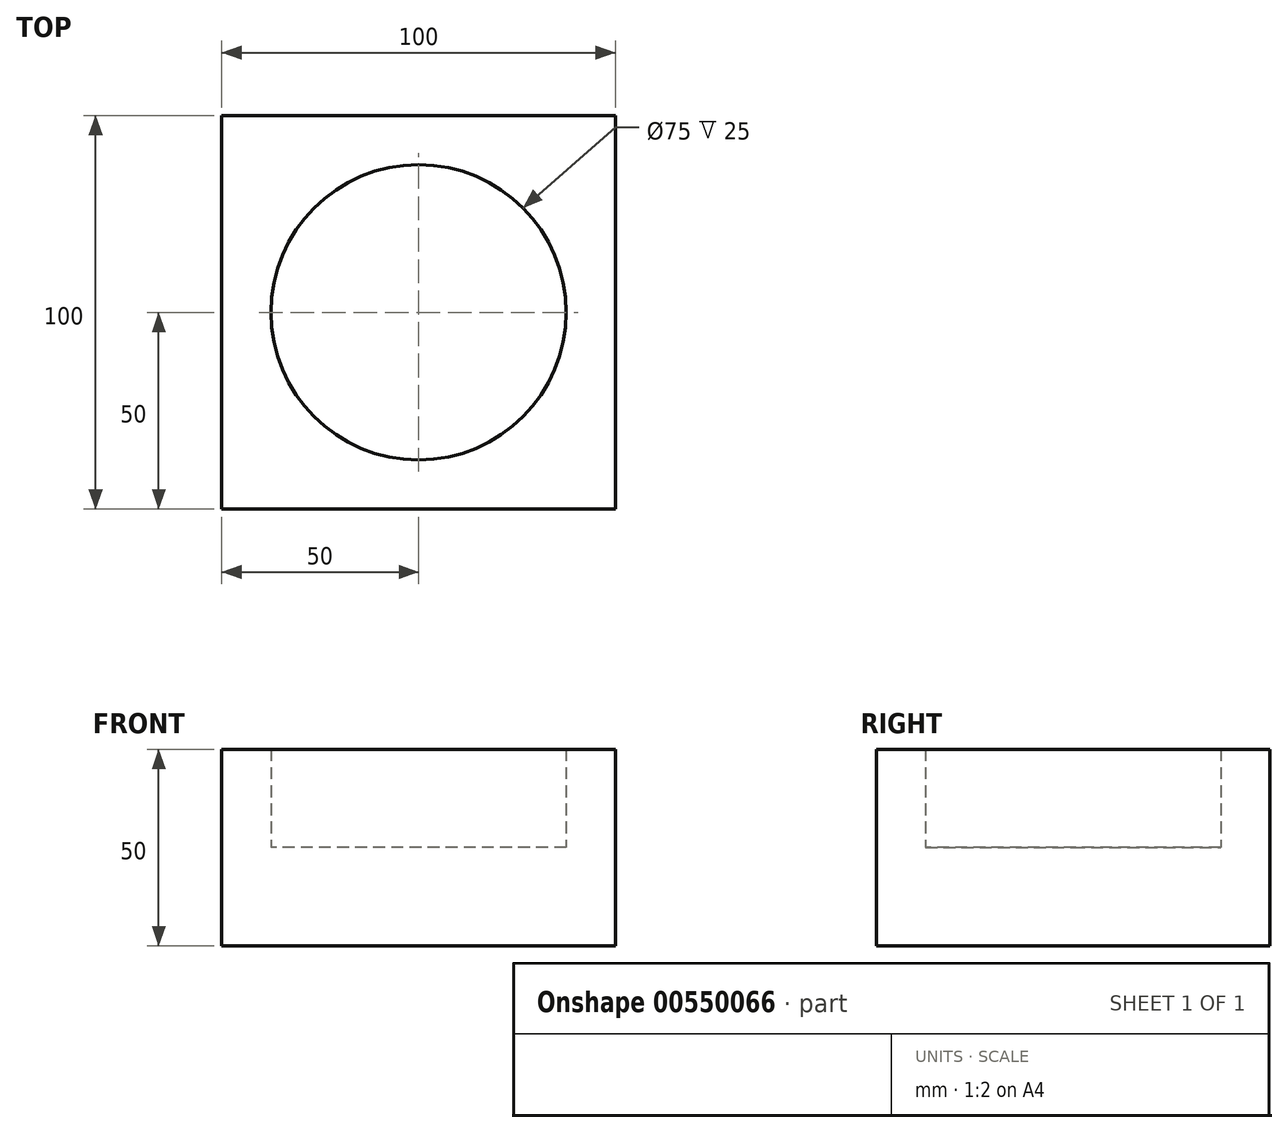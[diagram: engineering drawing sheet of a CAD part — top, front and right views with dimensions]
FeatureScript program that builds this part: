
annotation { "Feature Type Name" : "Feature", "Feature Type Description" : "" }
export const myFeature = defineFeature(function(context is Context, id is Id, definition is map)
    precondition{}
    {
        {
            var Q0;
            Q0=qCreatedBy(makeId("Top.planeOp"),FACE);
            var sketch = newSketch(context, id + "F0", { "sketchPlane" : qUnion([Q0])});
            skLineSegment(sketch, "E0.bottom", {"start": v(50, -50) * mm, "end": v(-50, -50) * mm});
            skLineSegment(sketch, "E0.top", {"start": v(50, 50) * mm, "end": v(-50, 50) * mm});
            skLineSegment(sketch, "E0.left", {"start": v(50, -50) * mm, "end": v(50, 50) * mm});
            skLineSegment(sketch, "E0.right", {"start": v(-50, -50) * mm, "end": v(-50, 50) * mm});
            skPoint(sketch, "E0.middle", {"position": v(0, 0) * mm});
            skCircle(sketch, "E1", {"center": v(0, 0) * mm, "radius": 37.5 * mm});
            skSolve(sketch);
        }
        {
            var Q0;
            Q0=makeQuery(id+"F0.imprint","IMPRINT",FACE,{"disambiguationData":[TD([[makeQuery(id+"F0.imprint","IMPRINT",EDGE,{"derivedFrom":sQuery(id+"F0.wireOp",EDGE,"E0.bottom")}),-1.0]])]});
            extrude(context, id + "F1", {"entities" : qUnion([Q0]), "depth" : 50 * mm, "offsetDistance" : 25 * mm});
        }
        {
            var Q0;
            Q0 = qSketchRegion(id + "F0", true);
            var Q1;
            Q1=makeQuery(id+"F0.imprint","IMPRINT",FACE,{"disambiguationData":[TD([[makeQuery(id+"F0.imprint","IMPRINT",EDGE,{"derivedFrom":sQuery(id+"F0.wireOp",EDGE,"E1")}),1.0]])]});
            extrude(context, id + "F2", {"entities" : qUnion([Q0, Q1]), "operationType" : NewBodyOperationType.ADD, "depth" : 25 * mm, "offsetDistance" : 25 * mm});
        }
    });
